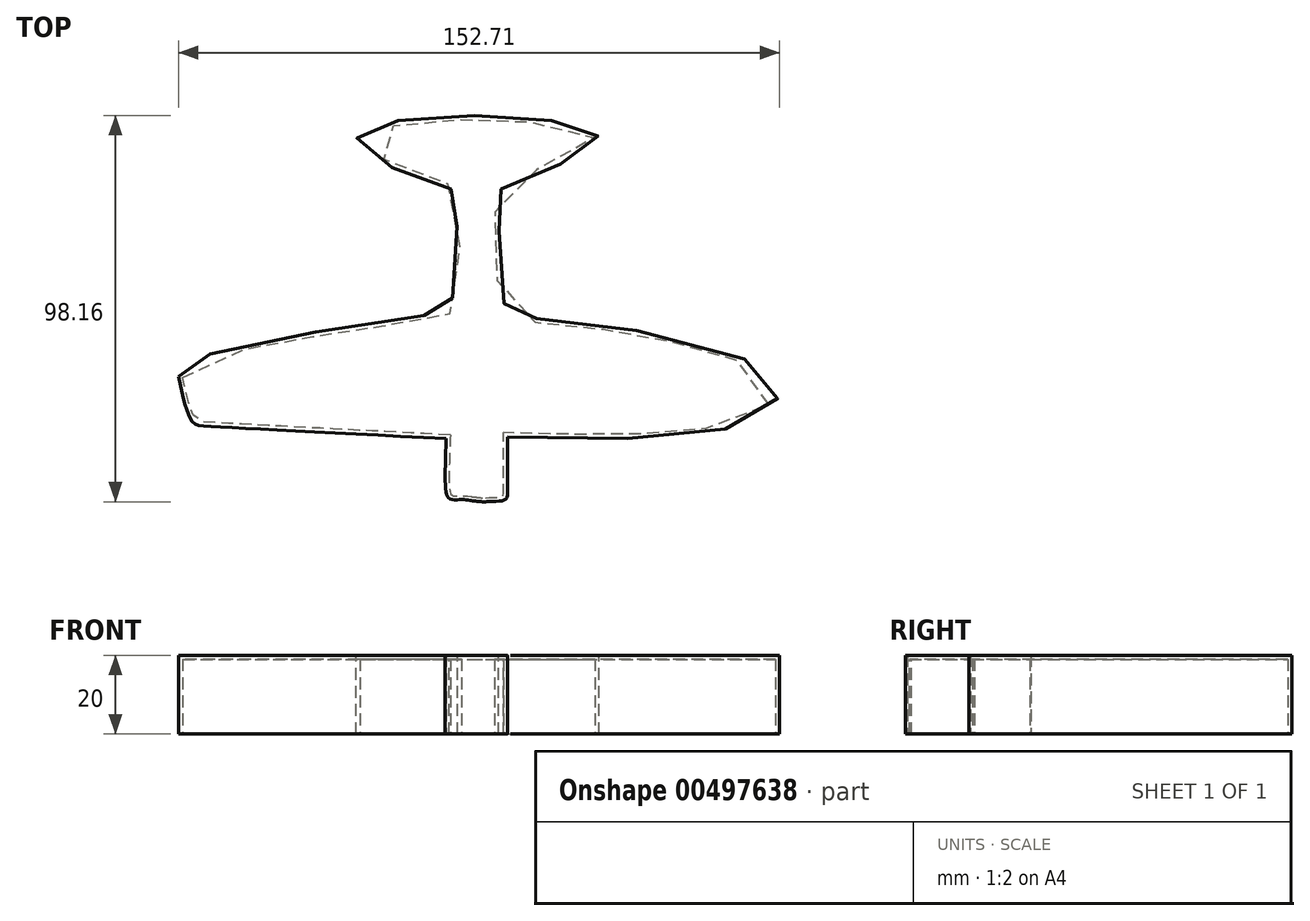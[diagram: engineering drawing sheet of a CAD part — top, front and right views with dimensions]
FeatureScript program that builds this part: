
annotation { "Feature Type Name" : "Feature", "Feature Type Description" : "" }
export const myFeature = defineFeature(function(context is Context, id is Id, definition is map)
    precondition{}
    {
        {
            var Q0;
            Q0=qCreatedBy(makeId("Top.planeOp"),FACE);
            var sketch = newSketch(context, id + "F0", { "sketchPlane" : qUnion([Q0])});
            skFitSpline(sketch, "E0", {"points": [v(-75.82, -7.77) * mm, v(-69.9, -2.84) * mm, v(-8.26, 8.75) * mm, v(-6.24, 11.41) * mm, v(-5.06, 38.07) * mm, v(-7.27, 40.07) * mm, v(-29.96, 50.42) * mm, v(-28.97, 54.37) * mm, v(-2.84, 58.56) * mm, v(27.99, 55.1) * mm, v(30.7, 51.66) * mm, v(6.79, 40.17) * mm, v(5.55, 37.6) * mm, v(7.27, 9.74) * mm, v(15.16, 7.03) * mm, v(75.33, -7.77) * mm, v(71.87, -17.88) * mm, v(7.77, -23.05) * mm], "startDerivative": vector(86.88, 108.9) * mm, "endDerivative": vector(-723.37, 19.85) * mm});
            skFitSpline(sketch, "E1", {"points": [v(-7.77, -23.55) * mm, v(-68.67, -20.34) * mm, v(-72.37, -19.1) * mm, v(-75.82, -7.77) * mm], "startDerivative": vector(-134.16, 6.9) * mm, "endDerivative": vector(-12.1, 54.9) * mm});
            skFitSpline(sketch, "E2", {"points": [v(-7.77, -23.55) * mm, v(-7.77, -37.28) * mm, v(-6.71, -38.93) * mm, v(-3.97, -39.04) * mm, v(-1.66, -39.25) * mm, v(1.96, -39.59) * mm, v(3.61, -39.48) * mm, v(7.13, -39.04) * mm, v(7.79, -36.73) * mm, v(7.77, -23.05) * mm], "startDerivative": vector(-3.61, -94.3) * mm, "endDerivative": vector(0, 90.98) * mm});
            skLineSegment(sketch, "E3", {"start": v(-1.66, -39.25) * mm, "end": v(-1.66, -7.5) * mm});
            skLineSegment(sketch, "E4", {"start": v(-1.66, -7.5) * mm, "end": v(2.19, -7.5) * mm});
            skLineSegment(sketch, "E5", {"start": v(2.19, -7.5) * mm, "end": v(2.19, -39.59) * mm});
            skSolve(sketch);
        }
        {
            var Q0;
            Q0 = qSketchRegion(id + "F0", true);
            extrude(context, id + "F1", {"entities" : qUnion([Q0]), "depth" : 20 * mm});
        }
        {
            var Q0;
            Q0=makeQuery(id+"F1.opExtrude","CAP_FACE",FACE,{"disambiguationData":[OSD([sQuery(id+"F0.wireOp",EDGE,"E0"),sQuery(id+"F0.wireOp",EDGE,"E1"),sQuery(id+"F0.wireOp",EDGE,"E2"),sQuery(id+"F0.wireOp",EDGE,"E3"),sQuery(id+"F0.wireOp",EDGE,"E4"),sQuery(id+"F0.wireOp",EDGE,"E5"),sQuery(id+"F0.wireOp",EDGE,"E2")])],"isStart":true});
            shell(context, id + "F2", {"entities" : qUnion([Q0]), "thickness" : 1 * mm});
        }
    });
